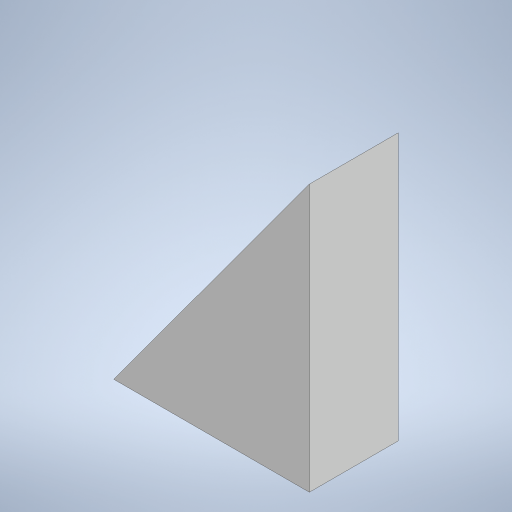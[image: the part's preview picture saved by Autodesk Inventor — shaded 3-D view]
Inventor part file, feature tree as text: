
AUTODESK INVENTOR PART (.ipt)
format: ipt  version: 2023.2 (Build 272271030, 271C)  size: 207,872 bytes
history: native  units: mm
features: extrude x1, sketch x1
ambient origin geometry x8: Origin, YZ Plane, XZ Plane, XY Plane, X Axis, Y Axis, Z Axis, Center Point
bodies: Solid1 (feature_tree)
feature tree (2):
  extrude  "Extrusion1"  Depth=10.0mm
  sketch  "Sketch1"  dims[d0=22.0mm d1=30.0mm d2=10.0mm d3=0.0mm]
